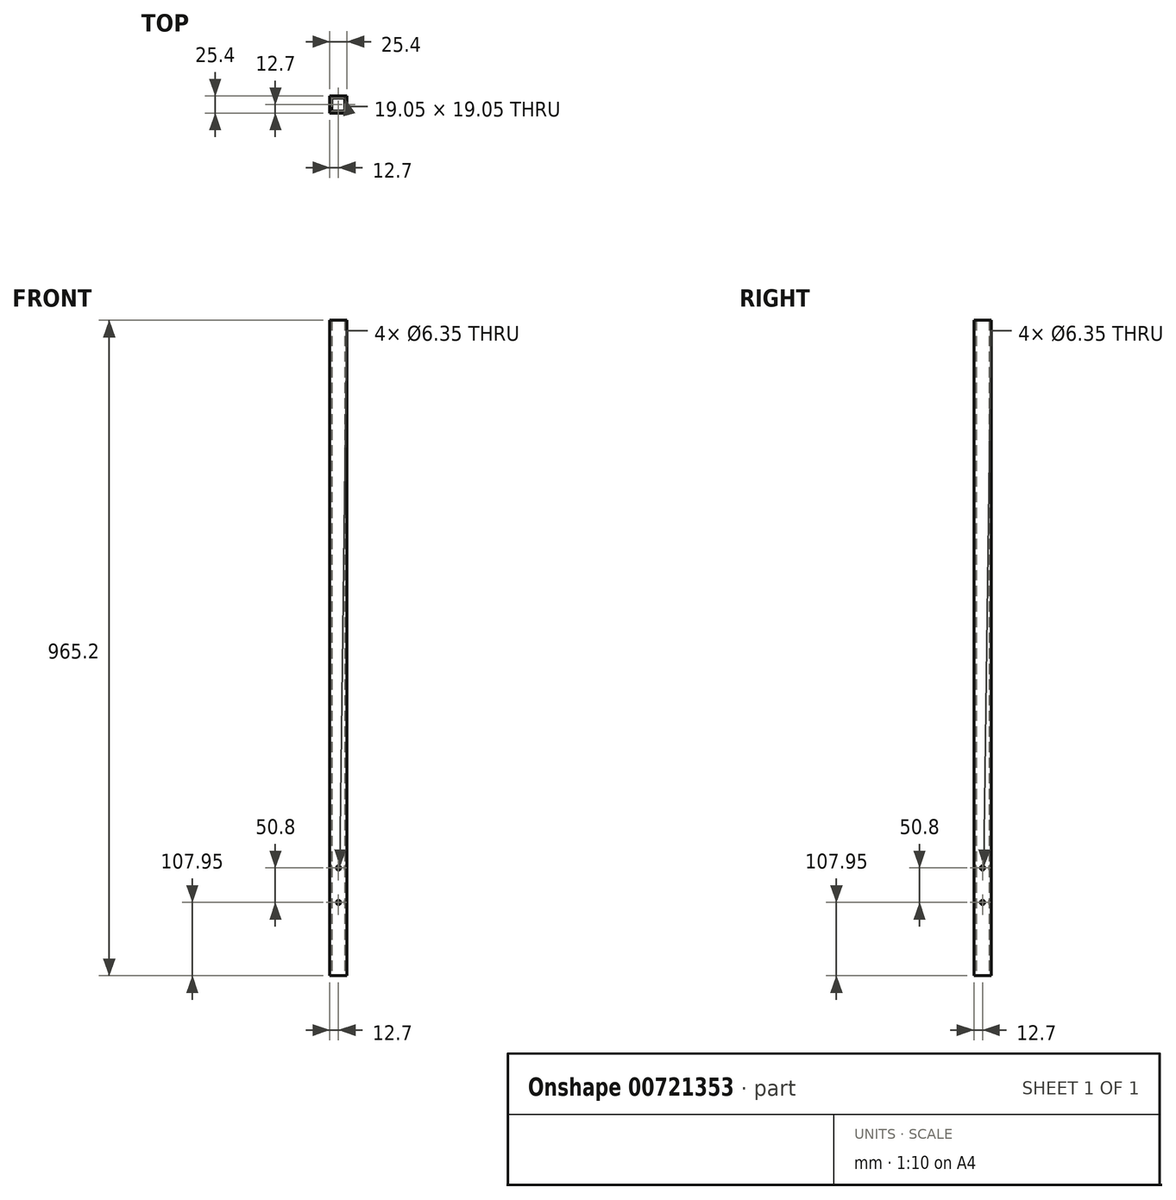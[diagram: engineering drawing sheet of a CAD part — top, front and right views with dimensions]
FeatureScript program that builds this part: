
annotation { "Feature Type Name" : "Feature", "Feature Type Description" : "" }
export const myFeature = defineFeature(function(context is Context, id is Id, definition is map)
    precondition{}
    {
        {
            var Q0;
            Q0=qCreatedBy(makeId("Top.planeOp"),FACE);
            var sketch = newSketch(context, id + "F0", { "sketchPlane" : qUnion([Q0])});
            skLineSegment(sketch, "E0.bottom", {"start": v(12.7, 12.7) * mm, "end": v(-12.7, 12.7) * mm});
            skLineSegment(sketch, "E0.top", {"start": v(12.7, -12.7) * mm, "end": v(-12.7, -12.7) * mm});
            skLineSegment(sketch, "E0.left", {"start": v(12.7, 12.7) * mm, "end": v(12.7, -12.7) * mm});
            skLineSegment(sketch, "E0.right", {"start": v(-12.7, 12.7) * mm, "end": v(-12.7, -12.7) * mm});
            skPoint(sketch, "E0.middle", {"position": v(0, 0) * mm});
            skLineSegment(sketch, "E1.0", {"start": v(9.53, -9.52) * mm, "end": v(-9.53, -9.52) * mm});
            skLineSegment(sketch, "E1.1", {"start": v(9.53, 9.53) * mm, "end": v(9.53, -9.52) * mm});
            skLineSegment(sketch, "E1.2", {"start": v(9.53, 9.53) * mm, "end": v(-9.53, 9.53) * mm});
            skLineSegment(sketch, "E1.3", {"start": v(-9.53, 9.53) * mm, "end": v(-9.53, -9.52) * mm});
            skSolve(sketch);
        }
        {
            var Q0;
            Q0 = qSketchRegion(id + "F0", true);
            extrude(context, id + "F1", {"entities" : qUnion([Q0]), "depth" : 965.2 * mm, "offsetDistance" : 25.4 * mm});
        }
        {
            var Q0;
            Q0=makeQuery(id+"F1.opExtrude","SWEPT_FACE",FACE,{"disambiguationData":[OSD([sQuery(id+"F0.wireOp",EDGE,"E0.right")])]});
            var sketch = newSketch(context, id + "F2", { "sketchPlane" : qUnion([Q0])});
            skCircle(sketch, "E2", {"center": v(0, 107.95) * mm, "radius": 3.18 * mm});
            skCircle(sketch, "E3", {"center": v(0, 158.75) * mm, "radius": 3.18 * mm});
            skSolve(sketch);
        }
        {
            var Q0;
            Q0 = qSketchRegion(id + "F2", true);
            extrude(context, id + "F3", {"entities" : qUnion([Q0]), "operationType" : NewBodyOperationType.REMOVE, "endBound" : BoundingType.THROUGH_ALL, "oppositeDirection" : true, "depth" : 25.4 * mm, "offsetDistance" : 25.4 * mm});
        }
        {
            var Q0;
            Q0=makeQuery(id+"F1.opExtrude","SWEPT_FACE",FACE,{"disambiguationData":[OSD([sQuery(id+"F0.wireOp",EDGE,"E0.top")])]});
            var sketch = newSketch(context, id + "F4", { "sketchPlane" : qUnion([Q0])});
            skCircle(sketch, "E4", {"center": v(0, 107.95) * mm, "radius": 3.18 * mm});
            skCircle(sketch, "E5", {"center": v(0, 158.75) * mm, "radius": 3.18 * mm});
            skPoint(sketch, "E5.centerSnap0", {"position": v(0, 0) * mm});
            skSolve(sketch);
        }
        {
            var Q0;
            Q0 = qSketchRegion(id + "F4", true);
            extrude(context, id + "F5", {"entities" : qUnion([Q0]), "operationType" : NewBodyOperationType.REMOVE, "endBound" : BoundingType.THROUGH_ALL, "oppositeDirection" : true, "depth" : 25.4 * mm, "offsetDistance" : 25.4 * mm});
        }
    });
